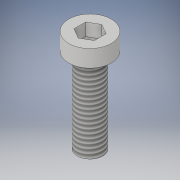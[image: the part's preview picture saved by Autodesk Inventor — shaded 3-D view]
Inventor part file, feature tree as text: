
AUTODESK INVENTOR PART (.ipt)
format: ipt  version: 2019 (Build 230136000, 136)  size: 124,928 bytes
history: native  units: mm
features: extrude x3, sketch x3, other x2
ambient origin geometry x8: Origin, YZ Plane, XZ Plane, XY Plane, X Axis, Y Axis, Z Axis, Center Point
bodies: Body1 (feature_tree)
feature tree (8):
  other  "實體1"
  extrude  "擠出1"  Depth=6.0mm
  other  "螺紋1"
  extrude  "擠出2"  Depth=20.0mm TaperAngle=0.0deg
  extrude  "擠出3"  Depth=10.0mm TaperAngle=0.0deg
  sketch  "草圖1"
  sketch  "草圖2"
  sketch  "草圖3"
